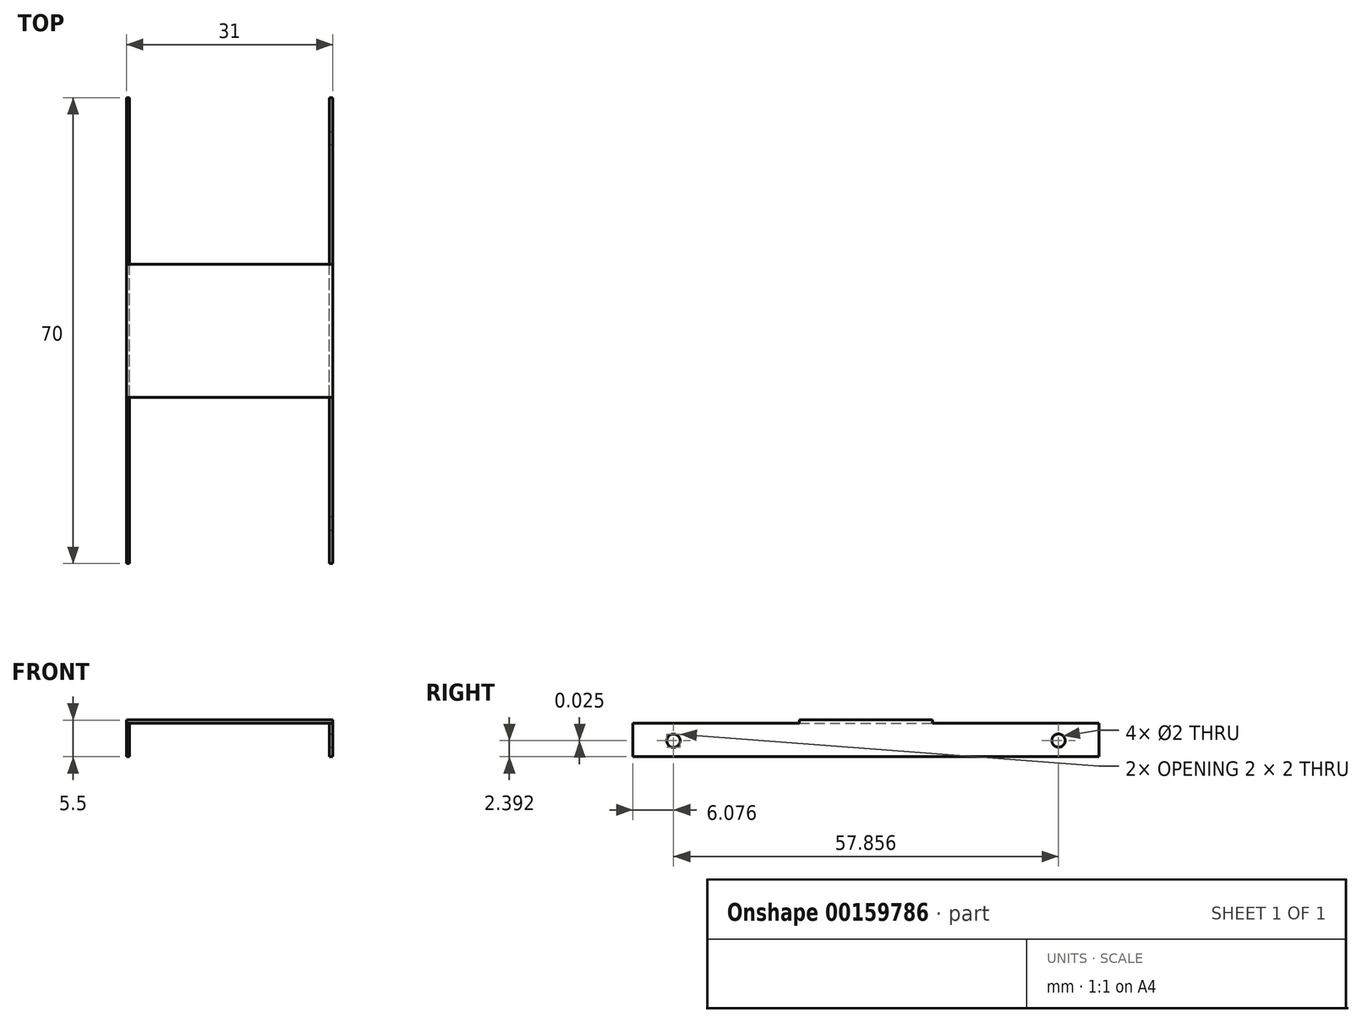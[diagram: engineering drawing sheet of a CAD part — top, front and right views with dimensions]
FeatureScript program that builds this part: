
annotation { "Feature Type Name" : "Feature", "Feature Type Description" : "" }
export const myFeature = defineFeature(function(context is Context, id is Id, definition is map)
    precondition{}
    {
        {
            var Q0;
            Q0=qCreatedBy(makeId("Front.planeOp"),FACE);
            var sketch = newSketch(context, id + "F0", { "sketchPlane" : qUnion([Q0])});
            skLineSegment(sketch, "E0", {"start": v(-60.85, 40.75) * mm, "end": v(-60.85, 45.75) * mm});
            skLineSegment(sketch, "E1", {"start": v(-30.85, 45.75) * mm, "end": v(-60.85, 45.75) * mm});
            skLineSegment(sketch, "E2", {"start": v(-30.85, 45.75) * mm, "end": v(-30.85, 40.75) * mm});
            skLineSegment(sketch, "E3", {"start": v(-30.85, 40.75) * mm, "end": v(-30.35, 40.75) * mm});
            skLineSegment(sketch, "E4", {"start": v(-30.35, 40.75) * mm, "end": v(-30.35, 46.25) * mm});
            skLineSegment(sketch, "E5", {"start": v(-30.35, 46.25) * mm, "end": v(-61.35, 46.25) * mm});
            skLineSegment(sketch, "E6", {"start": v(-61.35, 46.25) * mm, "end": v(-61.35, 40.75) * mm});
            skLineSegment(sketch, "E7", {"start": v(-61.35, 40.75) * mm, "end": v(-60.85, 40.75) * mm});
            skLineSegment(sketch, "E8", {"start": v(-60.85, 45.75) * mm, "end": v(-61.35, 45.75) * mm});
            skLineSegment(sketch, "E9", {"start": v(-30.85, 45.75) * mm, "end": v(-30.35, 45.75) * mm});
            skSolve(sketch);
        }
        {
            var Q0;
            Q0=makeQuery(id+"F0.imprint","IMPRINT",FACE,{"disambiguationData":[TD([[makeQuery(id+"F0.imprint","IMPRINT",EDGE,{"derivedFrom":sQuery(id+"F0.wireOp",EDGE,"E0")}),1.0]])]});
            var Q1;
            Q1=makeQuery(id+"F0.imprint","IMPRINT",FACE,{"disambiguationData":[TD([[makeQuery(id+"F0.imprint","IMPRINT",EDGE,{"derivedFrom":sQuery(id+"F0.wireOp",EDGE,"E1")}),-1.0]])]});
            var Q2;
            Q2=makeQuery(id+"F0.imprint","IMPRINT",FACE,{"disambiguationData":[TD([[makeQuery(id+"F0.imprint","IMPRINT",EDGE,{"derivedFrom":sQuery(id+"F0.wireOp",EDGE,"E2")}),1.0]])]});
            extrude(context, id + "F1", {"entities" : qUnion([Q0, Q1, Q2]), "depth" : 70 * mm});
        }
        {
            var Q0;
            Q0=makeQuery(id+"F0.imprint","IMPRINT",FACE,{"disambiguationData":[TD([[makeQuery(id+"F0.imprint","IMPRINT",EDGE,{"derivedFrom":sQuery(id+"F0.wireOp",EDGE,"E1")}),-1.0]])]});
            extrude(context, id + "F2", {"entities" : qUnion([Q0]), "operationType" : NewBodyOperationType.REMOVE, "depth" : 25 * mm});
        }
        {
            var Q0;
            Q0=makeQuery(id+"F0.imprint","IMPRINT",FACE,{"disambiguationData":[TD([[makeQuery(id+"F0.imprint","IMPRINT",EDGE,{"derivedFrom":sQuery(id+"F0.wireOp",EDGE,"E1")}),-1.0]])]});
            extrude(context, id + "F3", {"entities" : qUnion([Q0]), "operationType" : NewBodyOperationType.REMOVE, "depth" : 70 * mm, "hasSecondDirection" : true, "secondDirectionOppositeDirection" : false, "secondDirectionDepth" : 45 * mm});
        }
        {
            var Q0;
            Q0=qCreatedBy(makeId("Right.planeOp"),FACE);
            var sketch = newSketch(context, id + "F4", { "sketchPlane" : qUnion([Q0])});
            skCircle(sketch, "E10", {"center": v(-63.92, 43.14) * mm, "radius": 1 * mm});
            skSolve(sketch);
        }
        {
            var Q0;
            Q0=makeQuery(id+"F4.imprint","IMPRINT",FACE,{"disambiguationData":[TD([[makeQuery(id+"F4.imprint","IMPRINT",EDGE,{"derivedFrom":sQuery(id+"F4.wireOp",EDGE,"E10")}),1.0]])]});
            extrude(context, id + "F5", {"entities" : qUnion([Q0]), "operationType" : NewBodyOperationType.REMOVE, "oppositeDirection" : true, "depth" : 84.25 * mm});
        }
        {
            var Q0;
            Q0=qCreatedBy(makeId("Right.planeOp"),FACE);
            var sketch = newSketch(context, id + "F6", { "sketchPlane" : qUnion([Q0])});
            skCircle(sketch, "E11", {"center": v(-6.07, 43.17) * mm, "radius": 1 * mm});
            skSolve(sketch);
        }
        {
            var Q0;
            Q0=makeQuery(id+"F6.imprint","IMPRINT",FACE,{"disambiguationData":[TD([[makeQuery(id+"F6.imprint","IMPRINT",EDGE,{"derivedFrom":sQuery(id+"F6.wireOp",EDGE,"E11")}),1.0]])]});
            extrude(context, id + "F7", {"entities" : qUnion([Q0]), "operationType" : NewBodyOperationType.REMOVE, "oppositeDirection" : true, "depth" : 160.25 * mm});
        }
    });
